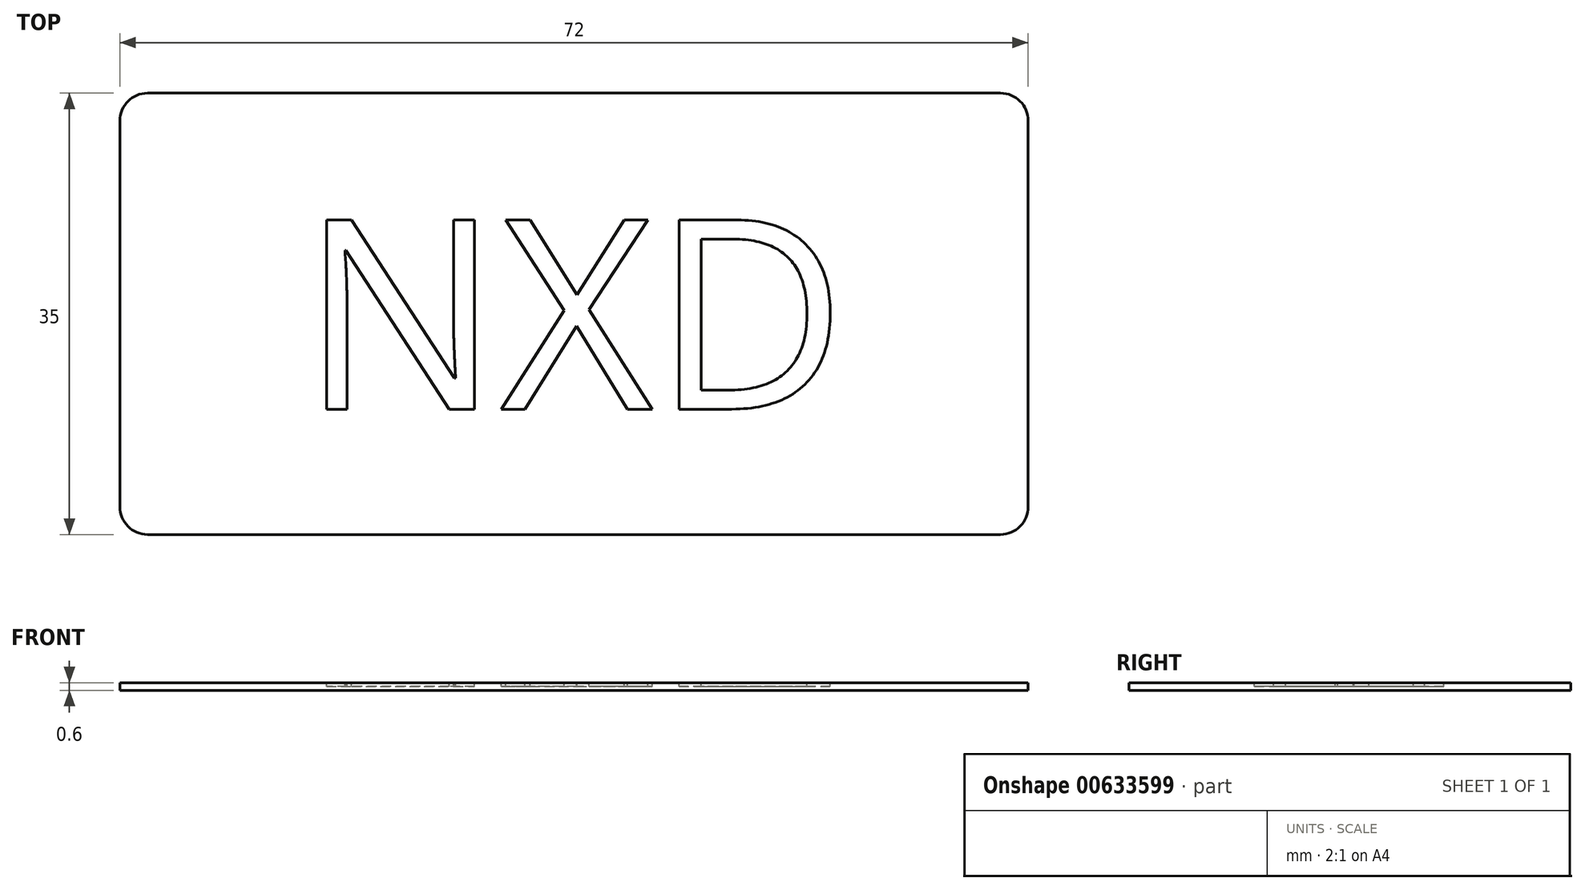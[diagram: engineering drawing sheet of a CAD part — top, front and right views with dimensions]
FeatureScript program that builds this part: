
annotation { "Feature Type Name" : "Feature", "Feature Type Description" : "" }
export const myFeature = defineFeature(function(context is Context, id is Id, definition is map)
    precondition{}
    {
        {
            var Q0;
            Q0=qCreatedBy(makeId("Top.planeOp"),FACE);
            var sketch = newSketch(context, id + "F0", { "sketchPlane" : qUnion([Q0])});
            skLineSegment(sketch, "E0.bottom", {"start": v(36, -17.5) * mm, "end": v(-36, -17.5) * mm});
            skLineSegment(sketch, "E0.top", {"start": v(36, 17.5) * mm, "end": v(-36, 17.5) * mm});
            skLineSegment(sketch, "E0.left", {"start": v(36, -17.5) * mm, "end": v(36, 17.5) * mm});
            skLineSegment(sketch, "E0.right", {"start": v(-36, -17.5) * mm, "end": v(-36, 17.5) * mm});
            skPoint(sketch, "E0.middle", {"position": v(0, 0) * mm});
            skSolve(sketch);
        }
        {
            var Q0;
            Q0=qSketchRegion(id+"F0",true);
            extrude(context, id + "F1", {"entities" : qUnion([Q0]), "depth" : 0.6 * mm});
        }
        {
            var Q0;
            Q0=makeQuery(id+"F1.opExtrude","CAP_FACE",FACE,{"disambiguationData":[OSD([sQuery(id+"F0.wireOp",EDGE,"E0.bottom"),sQuery(id+"F0.wireOp",EDGE,"E0.top"),sQuery(id+"F0.wireOp",EDGE,"E0.left"),sQuery(id+"F0.wireOp",EDGE,"E0.right")])],"isStart":false});
            var sketch = newSketch(context, id + "F2", { "sketchPlane" : qUnion([Q0])});
            skText(sketch, "E1", { "text": "NXD", "fontName": "OpenSans-Regular.ttf"});
            const initialGuessF2  = {"E1": [-0.02167, -0.00756, 1, 0, 0.01512]};
            skSetInitialGuess(sketch, initialGuessF2);
            skSolve(sketch);
        }
        {
            var Q0;
            Q0=makeQuery(id+"F2.imprint","IMPRINT",FACE,{"disambiguationData":[TD([[makeQuery(id+"F2.imprint","IMPRINT",EDGE,{"derivedFrom":sQuery(id+"F2.wireOp",EDGE,"E1.sketch_text.stroke-0")}),-1.0]])]});
            var Q1;
            Q1=qSketchRegion(id+"F2",true);
            extrude(context, id + "F3", {"entities" : qUnion([Q0, Q1]), "operationType" : NewBodyOperationType.REMOVE, "oppositeDirection" : true, "depth" : 0.3 * mm});
        }
        {
            var Q0;
            Q0=makeQuery(id+"F1.opExtrude","SWEPT_EDGE",EDGE,{"disambiguationData":[OSD([sQuery(id+"F0.wireOp",EDGE,"E0.bottom"),sQuery(id+"F0.wireOp",EDGE,"E0.right")])]});
            var Q1;
            Q1=makeQuery(id+"F1.opExtrude","SWEPT_EDGE",EDGE,{"disambiguationData":[OSD([sQuery(id+"F0.wireOp",EDGE,"E0.bottom"),sQuery(id+"F0.wireOp",EDGE,"E0.left")])]});
            var Q2;
            Q2=makeQuery(id+"F1.opExtrude","SWEPT_EDGE",EDGE,{"disambiguationData":[OSD([sQuery(id+"F0.wireOp",EDGE,"E0.top"),sQuery(id+"F0.wireOp",EDGE,"E0.left")])]});
            var Q3;
            Q3=makeQuery(id+"F1.opExtrude","SWEPT_EDGE",EDGE,{"disambiguationData":[OSD([sQuery(id+"F0.wireOp",EDGE,"E0.top"),sQuery(id+"F0.wireOp",EDGE,"E0.right")])]});
            fillet(context, id + "F4", {"entities" : qUnion([Q0, Q1, Q2, Q3]), "radius" : 2.2 * mm, "tangentPropagation" : true, "allowEdgeOverflow" : false});
        }
    });
